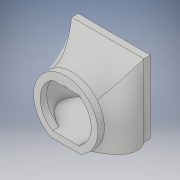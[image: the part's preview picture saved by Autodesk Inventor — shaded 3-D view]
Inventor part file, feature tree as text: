
AUTODESK INVENTOR PART (.ipt)
format: ipt  version: 2017 (Build 210142000, 142)  size: 409,088 bytes
history: native  units: in
note: dims shown in document units (in); Inventor stores cm internally (conversion verified against a paired STEP export)
features: sketch x4, extrude x3, other x2, loft x2
ambient origin geometry x8: Origin, YZ Plane, XZ Plane, XY Plane, X Axis, Y Axis, Z Axis, Center Point
bodies: Solid1 (feature_tree), Solid3 (feature_tree)
feature tree (11):
  extrude  "connection"  Depth=1.0in
  other  "front half of room"
  other  "front of room"
  sketch  "Sketch3"  dims[d17=2.7in d26=69.0in d27=59.0in d33=1.0in d34=1.0in]
  loft  "shell make "
  loft  "shell cut"
  extrude  "connection to door"  Depth=1.0in
  extrude  "light"  Depth=1.0in TaperAngle=0.0deg
  sketch  "Sketch1"  dims[d12=1.0in d13=0.0in d14=2.7in]
  sketch  "Sketch5"  dims[d35=1.0in d36=1.0in]
  sketch  "Sketch12"  dims[d55=100.0in d56=100.0in d57=1.0in d58=0.0in d82=4.0in d83=1.0in d84=4.8944in d85=0.5833in d86=3.8873in d87=3.8873in d88=1.7083in d89=0.0625in d90=0.0625in d91=1.6458in d92=0.125in d93=0.125in d153=6.21in d154=5.31in d157=0.0in d158=90.0deg d159=0.0in d160=90.0deg d161=0.0in d162=90.0deg d180=0.0in d181=90.0deg d182=0.0in d183=90.0deg d184=0.0in d185=90.0deg d217=3.082in d219=1.0in d220=1.0in d221=9.0in d222=9.0in d223=1.0in d233=0.25in d234=0.125in d235=45.0deg d236=0.0892in d237=0.0884in d238=0.0482in d239=1.0in d240=0.0in]
